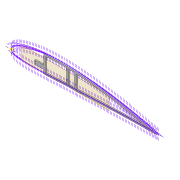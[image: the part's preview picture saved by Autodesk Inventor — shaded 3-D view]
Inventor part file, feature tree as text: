
AUTODESK INVENTOR PART (.ipt)
format: ipt  version: 2022 (Build 260153000, 153)  size: 429,568 bytes
history: native  units: mm
features: extrude x8, sketch x6, projected_geometry x6, fillet x2, shell x1, plane x1
ambient origin geometry x8: Origin, YZ Plane, XZ Plane, XY Plane, X Axis, Y Axis, Z Axis, Center Point
bodies: Solid1 (feature_tree)
feature tree (24):
  extrude  "Extrusion1"  Depth=5.0mm
  shell  "Shell1"  Thickness=2.0mm
  extrude  "Extrusion8"  Depth=5.9mm
  extrude  "Extrusion3"  Depth=10.0mm TaperAngle=0.0deg
  extrude  "Extrusion4"  Depth=2.0mm
  fillet  "Fillet1"  Radius=80.0mm
  extrude  "Extrusion5"  Depth=4.0mm TaperAngle=0.0deg
  plane  "Work Plane2"
  extrude  "Extrusion10"  Depth=0.2mm
  fillet  "Fillet2"  Radius=4.0mm
  extrude  "Extrusion9"  Depth=0.2mm
  extrude  "Extrusion11"  Depth=0.2mm
  sketch  "Sketch3"  dims[d0=4.0mm d1=0.0mm d2=5.0mm d7=2.0mm]
  sketch  "Sketch8"  dims[d8=2.0mm d9=5.9mm]
  sketch  "Sketch9"  dims[d13=10.0mm d14=0.0mm d16=10.0mm d17=0.0mm]
  projected_geometry  "Projected Loop4"
  projected_geometry  "Projected Loop10"
  sketch  "Sketch24"  dims[d22=4.0mm d23=0.0mm d31=2.0mm d62=80.0mm]
  projected_geometry  "Projected Loop11"
  projected_geometry  "Projected Loop12"
  projected_geometry  "Projected Loop13"
  sketch  "Sketch27"  dims[d63=6.0mm d64=4.0mm d65=0.0mm]
  projected_geometry  "Projected Loop14"
  sketch  "Sketch28"  dims[d66=3.0mm d67=12.0mm d72=4.0mm d73=0.0mm d74=12.0mm d75=30.0mm d76=3.05mm d77=5.0mm d78=10.0mm d79=0.0mm d80=2.0mm d84=6.0mm d86=6.0mm d87=20.0mm d88=2.1mm d89=2.1mm d90=3.0mm d91=3.0mm d92=0.2mm d93=10.0mm d94=0.0mm d95=100.0mm]
